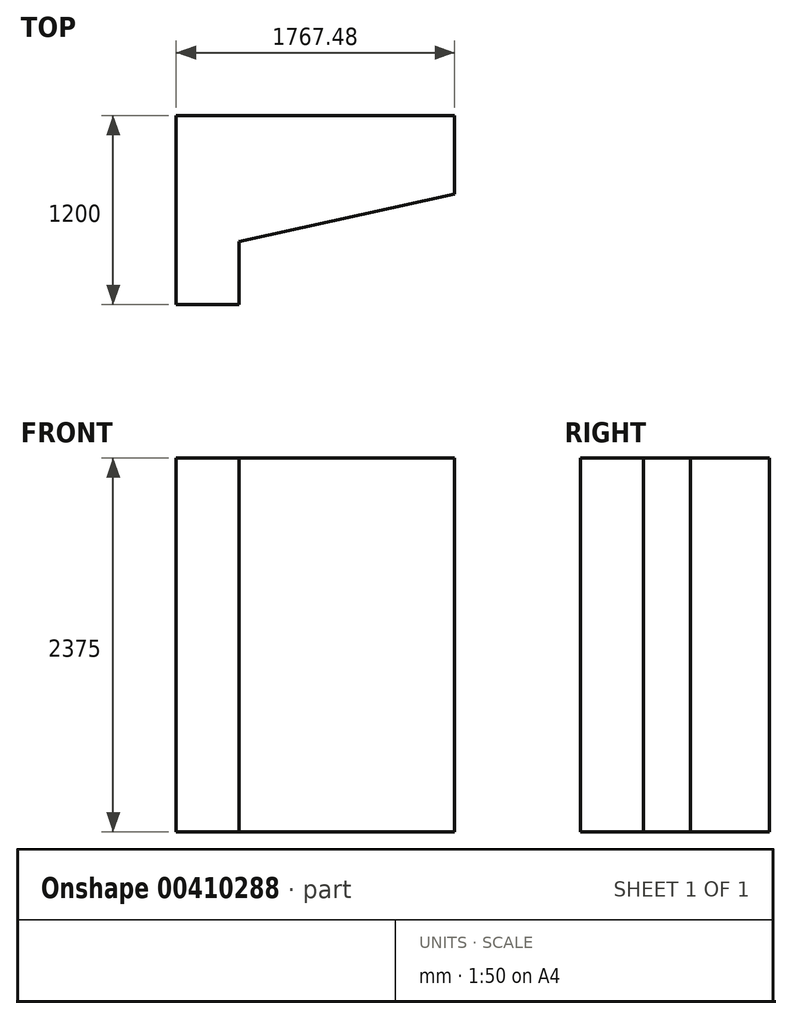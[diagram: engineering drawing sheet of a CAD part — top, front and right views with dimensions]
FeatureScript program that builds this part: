
annotation { "Feature Type Name" : "Feature", "Feature Type Description" : "" }
export const myFeature = defineFeature(function(context is Context, id is Id, definition is map)
    precondition{}
    {
        {
            var Q0;
            Q0=qCreatedBy(makeId("Top.planeOp"),FACE);
            var sketch = newSketch(context, id + "F0", { "sketchPlane" : qUnion([Q0])});
            skLineSegment(sketch, "E0.bottom", {"start": v(0, 0) * mm, "end": v(400, 0) * mm});
            skLineSegment(sketch, "E0.top", {"start": v(0, 1200) * mm, "end": v(1767.48, 1200) * mm});
            skLineSegment(sketch, "E0.left", {"start": v(0, 0) * mm, "end": v(0, 1200) * mm});
            skLineSegment(sketch, "E0.right", {"start": v(1767.48, 700) * mm, "end": v(1767.48, 1200) * mm});
            skLineSegment(sketch, "E1", {"start": v(400, 0) * mm, "end": v(400, 400) * mm});
            skLineSegment(sketch, "E2", {"start": v(400, 400) * mm, "end": v(1767.48, 700) * mm});
            skSolve(sketch);
        }
        {
            var Q0;
            Q0 = qSketchRegion(id + "F0", true);
            extrude(context, id + "F1", {"entities" : qUnion([Q0]), "depth" : 2375 * mm});
        }
    });
